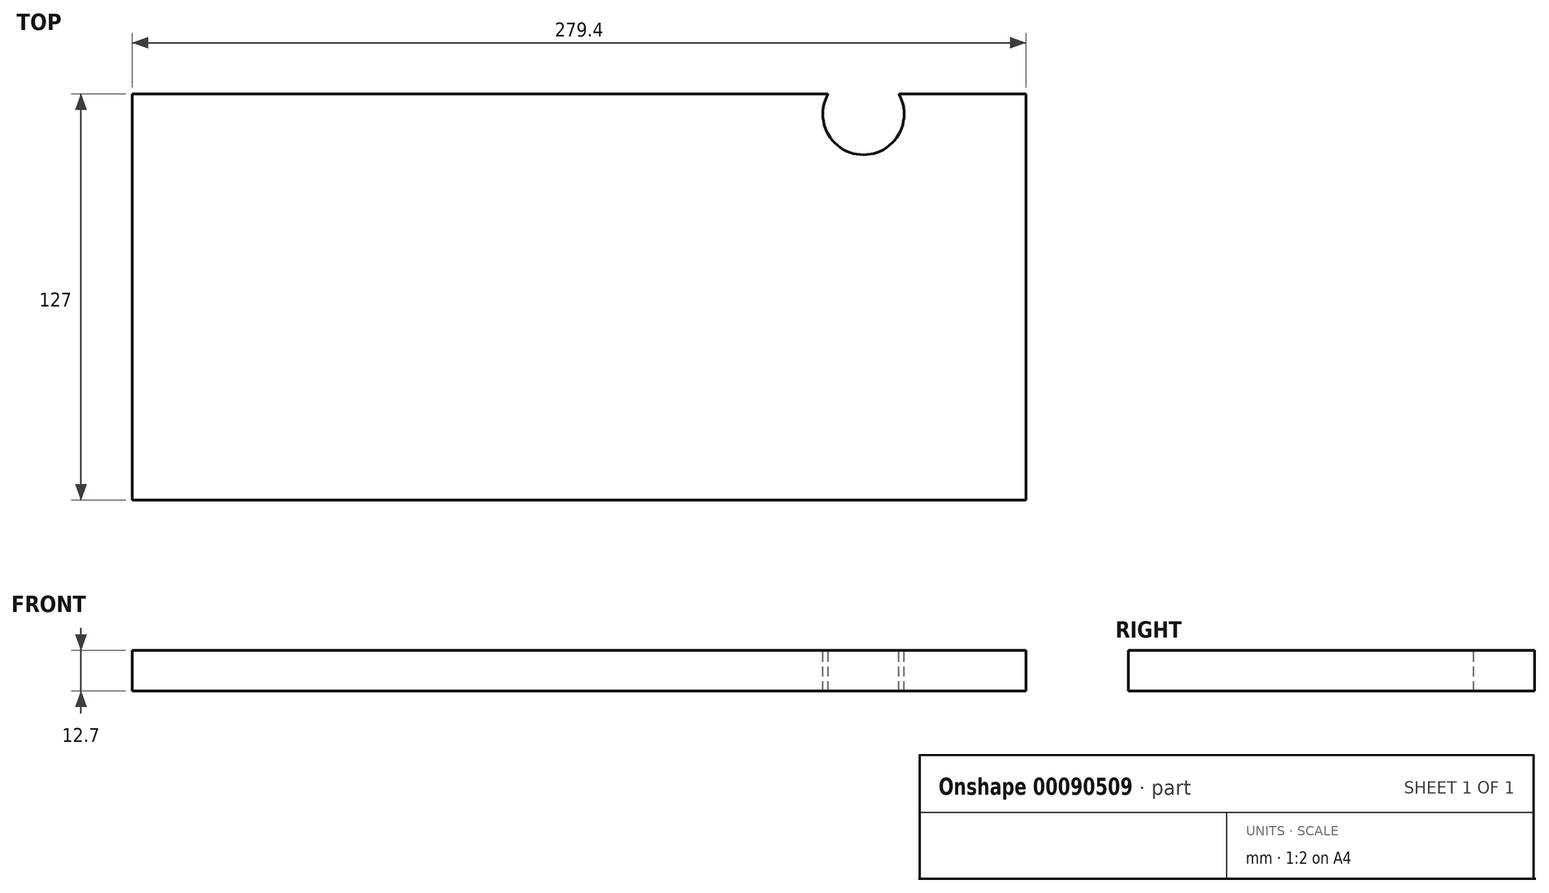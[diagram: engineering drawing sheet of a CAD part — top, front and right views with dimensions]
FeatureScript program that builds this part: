
annotation { "Feature Type Name" : "Feature", "Feature Type Description" : "" }
export const myFeature = defineFeature(function(context is Context, id is Id, definition is map)
    precondition{}
    {
        {
            var Q0;
            Q0=qCreatedBy(makeId("Top.planeOp"),FACE);
            var sketch = newSketch(context, id + "F0", { "sketchPlane" : qUnion([Q0])});
            skLineSegment(sketch, "E0.bottom", {"start": v(0, 0) * mm, "end": v(279.4, 0) * mm});
            skLineSegment(sketch, "E0.top", {"start": v(0, 127) * mm, "end": v(279.4, 127) * mm});
            skLineSegment(sketch, "E0.left", {"start": v(0, 0) * mm, "end": v(0, 127) * mm});
            skLineSegment(sketch, "E0.right", {"start": v(279.4, 0) * mm, "end": v(279.4, 127) * mm});
            skPoint(sketch, "E1.oppositeSnap0", {"position": v(139.7, 127) * mm});
            skLineSegment(sketch, "E1.bottom", {"start": v(279.4, 127) * mm, "end": v(139.7, 127) * mm});
            skLineSegment(sketch, "E1.top", {"start": v(279.4, 152.4) * mm, "end": v(139.7, 152.4) * mm});
            skLineSegment(sketch, "E1.left", {"start": v(279.4, 127) * mm, "end": v(279.4, 152.4) * mm});
            skLineSegment(sketch, "E1.right", {"start": v(139.7, 127) * mm, "end": v(139.7, 152.4) * mm});
            skSolve(sketch);
        }
        {
            var Q0;
            Q0=makeQuery(id+"F0.imprint","IMPRINT",FACE,{"disambiguationData":[TD([[makeQuery(id+"F0.imprint","IMPRINT",EDGE,{"derivedFrom":sQuery(id+"F0.wireOp",EDGE,"E0.bottom")}),1.0]])]});
            var Q1;
            Q1=makeQuery(id+"F0.imprint","IMPRINT",FACE,{"disambiguationData":[TD([[makeQuery(id+"F0.imprint","IMPRINT",EDGE,{"derivedFrom":sQuery(id+"F0.wireOp",EDGE,"E1.bottom")}),-1.0]])]});
            extrude(context, id + "F1", {"entities" : qUnion([Q0, Q1]), "depth" : 12.7 * mm});
        }
        {
            var Q0;
            Q0=makeQuery(id+"F1.opExtrude","CAP_FACE",FACE,{"disambiguationData":[OSD([sQuery(id+"F0.wireOp",EDGE,"E0.bottom"),sQuery(id+"F0.wireOp",EDGE,"E0.top"),sQuery(id+"F0.wireOp",EDGE,"E0.left"),sQuery(id+"F0.wireOp",EDGE,"E0.right")])],"isStart":false});
            var sketch = newSketch(context, id + "F2", { "sketchPlane" : qUnion([Q0])});
            skPoint(sketch, "E2.centerSnap0", {"position": v(279.4, 76.2) * mm});
            skCircle(sketch, "E3", {"center": v(228.6, 120.65) * mm, "radius": 12.7 * mm});
            skSolve(sketch);
        }
        {
            var Q0;
            Q0=makeQuery(id+"F2.imprint","IMPRINT",FACE,{"disambiguationData":[TD([[makeQuery(id+"F2.imprint","IMPRINT",EDGE,{"derivedFrom":sQuery(id+"F2.wireOp",EDGE,"E2")}),1.0]])]});
            var Q1;
            Q1=makeQuery(id+"F2.imprint","IMPRINT",FACE,{"disambiguationData":[TD([[makeQuery(id+"F2.imprint","IMPRINT",EDGE,{"derivedFrom":sQuery(id+"F2.wireOp",EDGE,"E3")}),1.0]])]});
            extrude(context, id + "F3", {"entities" : qUnion([Q0, Q1]), "operationType" : NewBodyOperationType.REMOVE, "endBound" : BoundingType.THROUGH_ALL, "oppositeDirection" : true, "depth" : 25.4 * mm});
        }
    });
